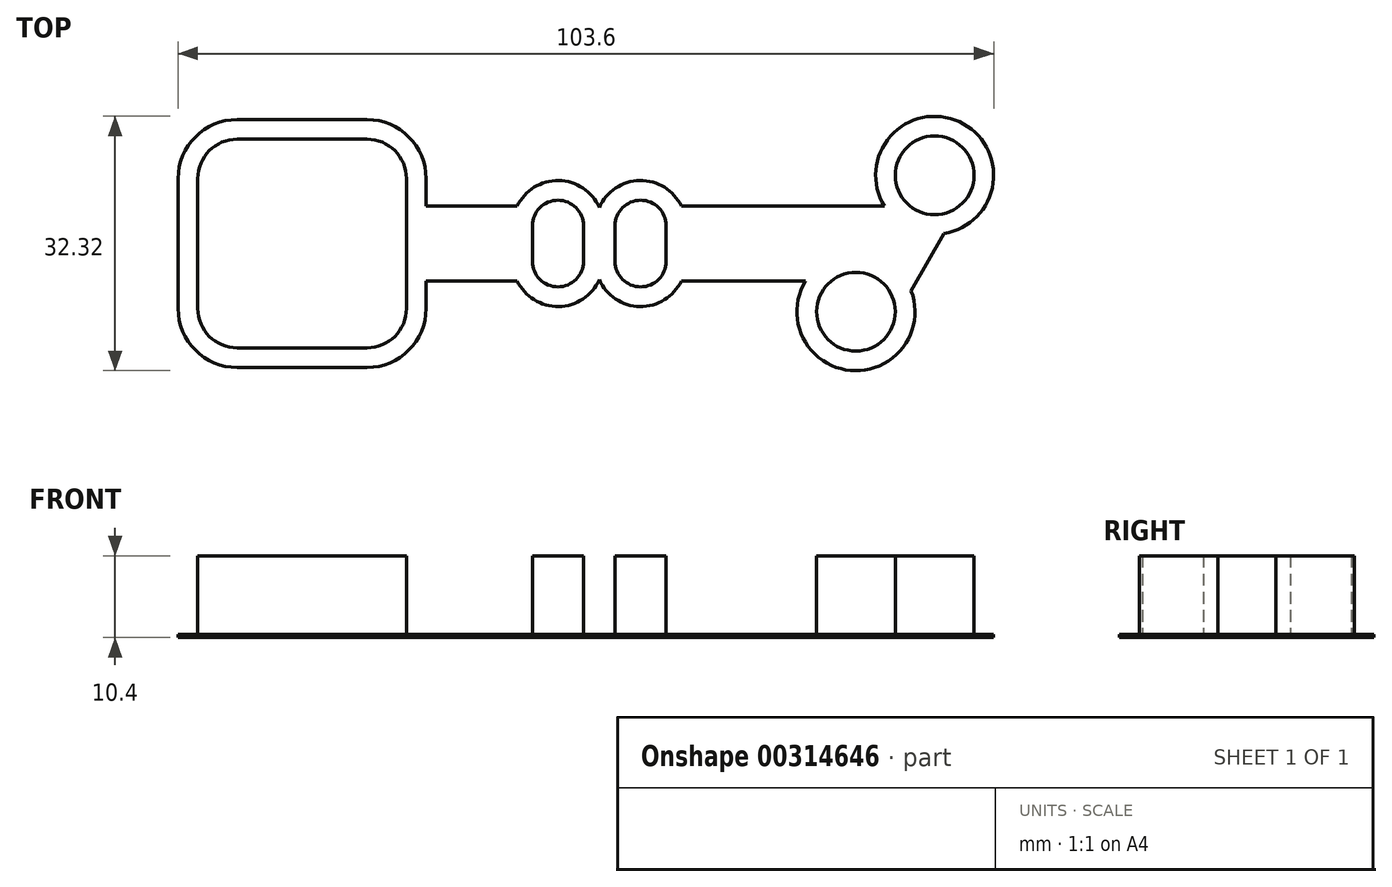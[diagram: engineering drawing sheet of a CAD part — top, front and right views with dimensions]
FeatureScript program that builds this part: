
annotation { "Feature Type Name" : "Feature", "Feature Type Description" : "" }
export const myFeature = defineFeature(function(context is Context, id is Id, definition is map)
    precondition{}
    {
        {
            var Q0;
            Q0=qCreatedBy(makeId("Top.planeOp"),FACE);
            var sketch = newSketch(context, id + "F0", { "sketchPlane" : qUnion([Q0])});
            skLineSegment(sketch, "E0.bottom", {"start": v(8.25, -13.25) * mm, "end": v(-8.25, -13.25) * mm});
            skLineSegment(sketch, "E0.top", {"start": v(8.25, 13.25) * mm, "end": v(-8.25, 13.25) * mm});
            skLineSegment(sketch, "E0.left", {"start": v(13.25, -8.25) * mm, "end": v(13.25, -4.5) * mm});
            skLineSegment(sketch, "E0.right", {"start": v(-13.25, -8.25) * mm, "end": v(-13.25, 8.25) * mm});
            skPoint(sketch, "E0.middle", {"position": v(0, 0) * mm});
            skPoint(sketch, "E1.visualSharp", {"position": v(-13.25, 13.25) * mm});
            skArc(sketch, "E1.filletArc", {"start": v(-8.25, 13.25) * mm, "mid": v(-11.79, 11.79) * mm, "end": v(-13.25, 8.25) * mm});
            skPoint(sketch, "E2.visualSharp", {"position": v(13.25, 13.25) * mm});
            skArc(sketch, "E2.filletArc", {"start": v(13.25, 8.25) * mm, "mid": v(11.79, 11.79) * mm, "end": v(8.25, 13.25) * mm});
            skPoint(sketch, "E3.visualSharp", {"position": v(13.25, -13.25) * mm});
            skArc(sketch, "E3.filletArc", {"start": v(8.25, -13.25) * mm, "mid": v(11.79, -11.79) * mm, "end": v(13.25, -8.25) * mm});
            skPoint(sketch, "E4.visualSharp", {"position": v(-13.25, -13.25) * mm});
            skArc(sketch, "E4.filletArc", {"start": v(-13.25, -8.25) * mm, "mid": v(-11.79, -11.79) * mm, "end": v(-8.25, -13.25) * mm});
            skCircle(sketch, "E5", {"center": v(0, 0) * mm, "radius": 4.5 * mm});
            skLineSegment(sketch, "E6", {"start": v(-4.5, 13.25) * mm, "end": v(-4.5, -13.25) * mm});
            skLineSegment(sketch, "E7", {"start": v(4.5, 13.25) * mm, "end": v(4.5, -13.25) * mm});
            skLineSegment(sketch, "E8", {"start": v(-13.25, 4.5) * mm, "end": v(13.25, 4.5) * mm});
            skLineSegment(sketch, "E9", {"start": v(-13.25, -4.5) * mm, "end": v(13.25, -4.5) * mm});
            skPoint(sketch, "E10.endSnap0", {"position": v(-4.5, 0) * mm});
            skLineSegment(sketch, "E11", {"start": v(13.25, 2.25) * mm, "end": v(29.25, 2.25) * mm});
            skLineSegment(sketch, "E12.bottom", {"start": v(29.25, 2.25) * mm, "end": v(35.75, 2.25) * mm});
            skLineSegment(sketch, "E12.top", {"start": v(29.25, -2.25) * mm, "end": v(35.75, -2.25) * mm});
            skLineSegment(sketch, "E12.left", {"start": v(29.25, 2.25) * mm, "end": v(29.25, -2.25) * mm});
            skLineSegment(sketch, "E12.right", {"start": v(35.75, 2.25) * mm, "end": v(35.75, -2.25) * mm});
            skLineSegment(sketch, "E13", {"start": v(37.75, 6.12) * mm, "end": v(37.75, -11.41) * mm, "construction": true});
            skLineSegment(sketch, "E14.MirrorCS", {"start": v(13.25, -2.25) * mm, "end": v(29.25, -2.25) * mm});
            skLineSegment(sketch, "E15.MirrorCS", {"start": v(39.75, 2.25) * mm, "end": v(39.75, -2.25) * mm});
            skLineSegment(sketch, "E16.MirrorCS", {"start": v(46.25, 2.25) * mm, "end": v(39.75, 2.25) * mm});
            skLineSegment(sketch, "E17.MirrorCS", {"start": v(85.23, 0) * mm, "end": v(-26.26, 0) * mm, "construction": true});
            skLineSegment(sketch, "E18.MirrorCS", {"start": v(46.25, -2.25) * mm, "end": v(39.75, -2.25) * mm});
            skLineSegment(sketch, "E19.MirrorCS", {"start": v(46.25, 2.25) * mm, "end": v(46.25, -2.25) * mm});
            skLineSegment(sketch, "E20", {"start": v(35.75, 2.25) * mm, "end": v(39.75, 2.25) * mm});
            skLineSegment(sketch, "E21", {"start": v(39.75, -2.25) * mm, "end": v(35.75, -2.25) * mm});
            skPoint(sketch, "E22", {"position": v(4.5, 0) * mm});
            skArc(sketch, "E23", {"start": v(29.25, 2.25) * mm, "mid": v(32.5, 5.5) * mm, "end": v(35.75, 2.25) * mm});
            skArc(sketch, "E24.MirrorCS", {"start": v(29.25, -2.25) * mm, "mid": v(32.5, -5.5) * mm, "end": v(35.75, -2.25) * mm});
            skArc(sketch, "E25.MirrorCS", {"start": v(46.25, 2.25) * mm, "mid": v(43, 5.5) * mm, "end": v(39.75, 2.25) * mm});
            skArc(sketch, "E26.MirrorCS", {"start": v(46.25, -2.25) * mm, "mid": v(43, -5.5) * mm, "end": v(39.75, -2.25) * mm});
            skLineSegment(sketch, "E27", {"start": v(80.35, 8.66) * mm, "end": v(70.35, -8.66) * mm, "construction": true});
            skPoint(sketch, "E28", {"position": v(75.35, 0) * mm});
            skLineSegment(sketch, "E29", {"start": v(76.17, 5.92) * mm, "end": v(76.17, 5.92) * mm});
            skLineSegment(sketch, "E30.MirrorCS", {"start": v(80.06, 3.67) * mm, "end": v(74.53, -5.92) * mm});
            skPoint(sketch, "E31", {"position": v(72.75, 0) * mm});
            skLineSegment(sketch, "E32", {"start": v(46.25, 2.25) * mm, "end": v(74.05, 2.25) * mm});
            skLineSegment(sketch, "E33", {"start": v(46.25, -2.25) * mm, "end": v(71.45, -2.25) * mm});
            skLineSegment(sketch, "E34", {"start": v(13.25, 4.5) * mm, "end": v(13.25, 8.25) * mm});
            skLineSegment(sketch, "E35", {"start": v(13.25, 2.25) * mm, "end": v(13.25, 4.5) * mm});
            skLineSegment(sketch, "E36", {"start": v(13.25, -2.25) * mm, "end": v(13.25, 2.25) * mm});
            skLineSegment(sketch, "E37", {"start": v(13.25, -4.5) * mm, "end": v(13.25, -2.25) * mm});
            skLineSegment(sketch, "E38", {"start": v(74.05, 2.25) * mm, "end": v(71.45, -2.25) * mm});
            skLineSegment(sketch, "E39", {"start": v(71.45, -2.25) * mm, "end": v(71.45, -2.25) * mm});
            skLineSegment(sketch, "E40", {"start": v(76.17, 5.92) * mm, "end": v(74.05, 2.25) * mm});
            skArc(sketch, "E41", {"start": v(76.17, 5.92) * mm, "mid": v(77.85, 4.33) * mm, "end": v(80.06, 3.67) * mm});
            skArc(sketch, "E42", {"start": v(76.1, 11.31) * mm, "mid": v(75.35, 8.6) * mm, "end": v(76.17, 5.92) * mm});
            skArc(sketch, "E43", {"start": v(80.06, 3.67) * mm, "mid": v(84.79, 10.96) * mm, "end": v(76.1, 11.31) * mm});
            skLineSegment(sketch, "E44", {"start": v(76.1, 11.31) * mm, "end": v(76.1, 11.31) * mm});
            skArc(sketch, "E45", {"start": v(74.53, -5.92) * mm, "mid": v(72.85, -4.33) * mm, "end": v(70.63, -3.67) * mm});
            skLineSegment(sketch, "E46", {"start": v(74.94, -10.64) * mm, "end": v(74.94, -10.64) * mm});
            skArc(sketch, "E47", {"start": v(74.94, -10.64) * mm, "mid": v(75.33, -8.23) * mm, "end": v(74.53, -5.92) * mm});
            skArc(sketch, "E48", {"start": v(70.63, -3.67) * mm, "mid": v(66.1, -11.29) * mm, "end": v(74.94, -10.64) * mm});
            skLineSegment(sketch, "E49", {"start": v(70.63, -3.67) * mm, "end": v(70.63, -3.67) * mm});
            skLineSegment(sketch, "E50", {"start": v(71.45, -2.25) * mm, "end": v(70.63, -3.67) * mm});
            skArc(sketch, "E51.0", {"start": v(15.75, 8.25) * mm, "mid": v(13.55, 13.55) * mm, "end": v(8.25, 15.75) * mm});
            skLineSegment(sketch, "E51.1", {"start": v(15.75, 4.75) * mm, "end": v(15.75, 8.25) * mm});
            skLineSegment(sketch, "E51.2", {"start": v(15.75, 4.75) * mm, "end": v(27.32, 4.75) * mm});
            skArc(sketch, "E51.3", {"start": v(27.32, 4.75) * mm, "mid": v(32.59, 8) * mm, "end": v(37.75, 4.6) * mm});
            skArc(sketch, "E51.4", {"start": v(48.18, 4.75) * mm, "mid": v(42.91, 8) * mm, "end": v(37.75, 4.6) * mm});
            skLineSegment(sketch, "E51.5", {"start": v(8.25, 15.75) * mm, "end": v(-8.25, 15.75) * mm});
            skLineSegment(sketch, "E51.6", {"start": v(48.18, 4.75) * mm, "end": v(73.95, 4.75) * mm});
            skArc(sketch, "E51.7", {"start": v(74, 12.64) * mm, "mid": v(72.85, 8.7) * mm, "end": v(73.95, 4.75) * mm});
            skArc(sketch, "E51.8", {"start": v(81.56, 1.26) * mm, "mid": v(86.6, 12.81) * mm, "end": v(74, 12.64) * mm});
            skLineSegment(sketch, "E51.9", {"start": v(81.56, 1.26) * mm, "end": v(77.36, -6) * mm});
            skArc(sketch, "E51.10", {"start": v(77.23, -11.64) * mm, "mid": v(77.85, -8.83) * mm, "end": v(77.36, -6) * mm});
            skArc(sketch, "E51.11", {"start": v(63.95, -4.75) * mm, "mid": v(66.9, -15.32) * mm, "end": v(77.23, -11.64) * mm});
            skLineSegment(sketch, "E51.12", {"start": v(8.25, -15.75) * mm, "end": v(-8.25, -15.75) * mm});
            skArc(sketch, "E51.13", {"start": v(-15.75, -8.25) * mm, "mid": v(-13.55, -13.55) * mm, "end": v(-8.25, -15.75) * mm});
            skLineSegment(sketch, "E51.14", {"start": v(-15.75, -8.25) * mm, "end": v(-15.75, 8.25) * mm});
            skArc(sketch, "E51.15", {"start": v(-8.25, 15.75) * mm, "mid": v(-13.55, 13.55) * mm, "end": v(-15.75, 8.25) * mm});
            skArc(sketch, "E51.16", {"start": v(8.25, -15.75) * mm, "mid": v(13.55, -13.55) * mm, "end": v(15.75, -8.25) * mm});
            skLineSegment(sketch, "E51.17", {"start": v(15.75, -8.25) * mm, "end": v(15.75, -4.75) * mm});
            skLineSegment(sketch, "E51.18", {"start": v(15.75, -4.75) * mm, "end": v(27.32, -4.75) * mm});
            skArc(sketch, "E51.19", {"start": v(27.32, -4.75) * mm, "mid": v(32.59, -8) * mm, "end": v(37.75, -4.6) * mm});
            skArc(sketch, "E51.20", {"start": v(48.18, -4.75) * mm, "mid": v(42.91, -8) * mm, "end": v(37.75, -4.6) * mm});
            skLineSegment(sketch, "E51.21", {"start": v(48.18, -4.75) * mm, "end": v(63.95, -4.75) * mm});
            skSolve(sketch);
        }
        {
            var Q0;
            {var subQ6=sQuery(id+"F0.wireOp",EDGE,"E2.filletArc");Q0=makeQuery(id+"F0.imprint","IMPRINT",FACE,{"disambiguationData":[TD([[makeQuery(id+"F0.imprint","IMPRINT",EDGE,{"derivedFrom":subQ6}),1.0]])]});}
            var Q1;
            {var subQ5=sQuery(id+"F0.wireOp",EDGE,"E1.filletArc");Q1=makeQuery(id+"F0.imprint","IMPRINT",FACE,{"disambiguationData":[TD([[makeQuery(id+"F0.imprint","IMPRINT",EDGE,{"derivedFrom":subQ5}),1.0]])]});}
            var Q2;
            {var subQ2=sQuery(id+"F0.wireOp",EDGE,"E6");var subQ5=sQuery(id+"F0.wireOp",EDGE,"E0.top");var subQ8=makeQuery(id+"F0.imprint","INTERSECT",VERTEX,{"derivedFrom":[subQ5,subQ2]});Q2=makeQuery(id+"F0.imprint","IMPRINT",FACE,{"disambiguationData":[TD([[makeQuery(id+"F0.imprint","IMPRINT",EDGE,{"disambiguationData":[TD([[subQ8,1.0]])],"derivedFrom":subQ5}),1.0]])]});}
            var Q3;
            {var subQ0=sQuery(id+"F0.wireOp",EDGE,"E8");var subQ1=sQuery(id+"F0.wireOp",EDGE,"E0.right");var subQ2=makeQuery(id+"F0.imprint","INTERSECT",VERTEX,{"derivedFrom":[subQ1,subQ0]});Q3=makeQuery(id+"F0.imprint","IMPRINT",FACE,{"disambiguationData":[TD([[makeQuery(id+"F0.imprint","IMPRINT",EDGE,{"disambiguationData":[TD([[subQ2,1.0]])],"derivedFrom":subQ1}),-1.0]])]});}
            var Q4;
            Q4=makeQuery(id+"F0.imprint","IMPRINT",FACE,{"disambiguationData":[TD([[makeQuery(id+"F0.imprint","IMPRINT",EDGE,{"derivedFrom":sQuery(id+"F0.wireOp",EDGE,"E12.top")}),-1.0]])]});
            var Q5;
            Q5=makeQuery(id+"F0.imprint","IMPRINT",FACE,{"disambiguationData":[TD([[makeQuery(id+"F0.imprint","IMPRINT",EDGE,{"derivedFrom":sQuery(id+"F0.wireOp",EDGE,"E11")}),-1.0]])]});
            var Q6;
            Q6=makeQuery(id+"F0.imprint","IMPRINT",FACE,{"disambiguationData":[TD([[makeQuery(id+"F0.imprint","IMPRINT",EDGE,{"derivedFrom":sQuery(id+"F0.wireOp",EDGE,"E12.bottom")}),1.0]])]});
            var Q7;
            Q7=makeQuery(id+"F0.imprint","IMPRINT",FACE,{"disambiguationData":[TD([[makeQuery(id+"F0.imprint","IMPRINT",EDGE,{"derivedFrom":sQuery(id+"F0.wireOp",EDGE,"E18.MirrorCS")}),1.0]])]});
            var Q8;
            {var subQ0=sQuery(id+"F0.wireOp",EDGE,"E35");Q8=makeQuery(id+"F0.imprint","IMPRINT",FACE,{"disambiguationData":[TD([[makeQuery(id+"F0.imprint","IMPRINT",EDGE,{"derivedFrom":subQ0}),1.0]])]});}
            var Q9;
            {var subQ1=sQuery(id+"F0.wireOp",EDGE,"E0.left");Q9=makeQuery(id+"F0.imprint","IMPRINT",FACE,{"disambiguationData":[TD([[makeQuery(id+"F0.imprint","IMPRINT",EDGE,{"derivedFrom":subQ1}),1.0]])]});}
            var Q10;
            {var subQ5=sQuery(id+"F0.wireOp",EDGE,"E4.filletArc");Q10=makeQuery(id+"F0.imprint","IMPRINT",FACE,{"disambiguationData":[TD([[makeQuery(id+"F0.imprint","IMPRINT",EDGE,{"derivedFrom":subQ5}),1.0]])]});}
            var Q11;
            Q11=makeQuery(id+"F0.imprint","IMPRINT",FACE,{"disambiguationData":[TD([[makeQuery(id+"F0.imprint","IMPRINT",EDGE,{"derivedFrom":sQuery(id+"F0.wireOp",EDGE,"E45")}),1.0]])]});
            var Q12;
            Q12=makeQuery(id+"F0.imprint","IMPRINT",FACE,{"disambiguationData":[TD([[makeQuery(id+"F0.imprint","IMPRINT",EDGE,{"derivedFrom":sQuery(id+"F0.wireOp",EDGE,"E0.left")}),-1.0]])]});
            var Q13;
            Q13=makeQuery(id+"F0.imprint","IMPRINT",FACE,{"disambiguationData":[TD([[makeQuery(id+"F0.imprint","IMPRINT",EDGE,{"derivedFrom":sQuery(id+"F0.wireOp",EDGE,"E41")}),1.0]])]});
            var Q14;
            Q14=makeQuery(id+"F0.imprint","IMPRINT",FACE,{"disambiguationData":[TD([[makeQuery(id+"F0.imprint","IMPRINT",EDGE,{"derivedFrom":sQuery(id+"F0.wireOp",EDGE,"E19.MirrorCS")}),1.0]])]});
            var Q15;
            Q15=makeQuery(id+"F0.imprint","IMPRINT",FACE,{"disambiguationData":[TD([[makeQuery(id+"F0.imprint","IMPRINT",EDGE,{"derivedFrom":sQuery(id+"F0.wireOp",EDGE,"E16.MirrorCS")}),-1.0]])]});
            var Q16;
            {var subQ1=sQuery(id+"F0.wireOp",EDGE,"E0.bottom");var subQ6=sQuery(id+"F0.wireOp",EDGE,"E6");var subQ8=makeQuery(id+"F0.imprint","INTERSECT",VERTEX,{"derivedFrom":[subQ1,subQ6]});Q16=makeQuery(id+"F0.imprint","IMPRINT",FACE,{"disambiguationData":[TD([[makeQuery(id+"F0.imprint","IMPRINT",EDGE,{"disambiguationData":[TD([[subQ8,1.0]])],"derivedFrom":subQ1}),-1.0]])]});}
            var Q17;
            Q17=makeQuery(id+"F0.imprint","IMPRINT",FACE,{"disambiguationData":[TD([[makeQuery(id+"F0.imprint","IMPRINT",EDGE,{"derivedFrom":sQuery(id+"F0.wireOp",EDGE,"E30.MirrorCS")}),-1.0]])]});
            var Q18;
            {var subQ0=sQuery(id+"F0.wireOp",EDGE,"E5");var subQ1=makeQuery(id+"F0.imprint","INTERSECT",VERTEX,{"derivedFrom":[subQ0,sQuery(id+"F0.wireOp",EDGE,"E8")]});Q18=makeQuery(id+"F0.imprint","IMPRINT",FACE,{"disambiguationData":[TD([[makeQuery(id+"F0.imprint","IMPRINT",EDGE,{"disambiguationData":[TD([[subQ1,1.0]])],"derivedFrom":subQ0}),1.0]])]});}
            var Q19;
            {var subQ0=sQuery(id+"F0.wireOp",EDGE,"E7");var subQ1=sQuery(id+"F0.wireOp",EDGE,"E5");var subQ2=makeQuery(id+"F0.imprint","INTERSECT",VERTEX,{"derivedFrom":[subQ1,subQ0]});Q19=makeQuery(id+"F0.imprint","IMPRINT",FACE,{"disambiguationData":[TD([[makeQuery(id+"F0.imprint","IMPRINT",EDGE,{"disambiguationData":[TD([[subQ2,1.0]])],"derivedFrom":subQ1}),-1.0]])]});}
            var Q20;
            {var subQ0=sQuery(id+"F0.wireOp",EDGE,"E8");var subQ1=sQuery(id+"F0.wireOp",EDGE,"E5");var subQ2=makeQuery(id+"F0.imprint","INTERSECT",VERTEX,{"derivedFrom":[subQ1,subQ0]});Q20=makeQuery(id+"F0.imprint","IMPRINT",FACE,{"disambiguationData":[TD([[makeQuery(id+"F0.imprint","IMPRINT",EDGE,{"disambiguationData":[TD([[subQ2,-1.0]])],"derivedFrom":subQ1}),-1.0]])]});}
            var Q21;
            {var subQ0=sQuery(id+"F0.wireOp",EDGE,"E6");var subQ1=sQuery(id+"F0.wireOp",EDGE,"E5");var subQ2=makeQuery(id+"F0.imprint","INTERSECT",VERTEX,{"derivedFrom":[subQ1,subQ0]});Q21=makeQuery(id+"F0.imprint","IMPRINT",FACE,{"disambiguationData":[TD([[makeQuery(id+"F0.imprint","IMPRINT",EDGE,{"disambiguationData":[TD([[subQ2,-1.0]])],"derivedFrom":subQ1}),-1.0]])]});}
            var Q22;
            {var subQ0=sQuery(id+"F0.wireOp",EDGE,"E8");var subQ1=sQuery(id+"F0.wireOp",EDGE,"E5");var subQ2=makeQuery(id+"F0.imprint","INTERSECT",VERTEX,{"derivedFrom":[subQ1,subQ0]});Q22=makeQuery(id+"F0.imprint","IMPRINT",FACE,{"disambiguationData":[TD([[makeQuery(id+"F0.imprint","IMPRINT",EDGE,{"disambiguationData":[TD([[subQ2,1.0]])],"derivedFrom":subQ1}),-1.0]])]});}
            var Q23;
            Q23=makeQuery(id+"F0.imprint","IMPRINT",FACE,{"disambiguationData":[TD([[makeQuery(id+"F0.imprint","IMPRINT",EDGE,{"derivedFrom":sQuery(id+"F0.wireOp",EDGE,"E12.bottom")}),-1.0]])]});
            var Q24;
            Q24=makeQuery(id+"F0.imprint","IMPRINT",FACE,{"disambiguationData":[TD([[makeQuery(id+"F0.imprint","IMPRINT",EDGE,{"derivedFrom":sQuery(id+"F0.wireOp",EDGE,"E12.right")}),1.0]])]});
            var Q25;
            Q25=makeQuery(id+"F0.imprint","IMPRINT",FACE,{"disambiguationData":[TD([[makeQuery(id+"F0.imprint","IMPRINT",EDGE,{"derivedFrom":sQuery(id+"F0.wireOp",EDGE,"E16.MirrorCS")}),1.0]])]});
            extrude(context, id + "F1", {"entities" : qUnion([Q0, Q1, Q2, Q3, Q4, Q5, Q6, Q7, Q8, Q9, Q10, Q11, Q12, Q13, Q14, Q15, Q16, Q17, Q18, Q19, Q20, Q21, Q22, Q23, Q24, Q25]), "depth" : 0.4 * mm});
        }
        {
            var Q0;
            Q0=makeQuery(id+"F1.opExtrude","CAP_FACE",FACE,{"disambiguationData":[OSD([sQuery(id+"F0.wireOp",EDGE,"E51.0"),sQuery(id+"F0.wireOp",EDGE,"E51.1"),sQuery(id+"F0.wireOp",EDGE,"E51.2"),sQuery(id+"F0.wireOp",EDGE,"E51.3"),sQuery(id+"F0.wireOp",EDGE,"E51.4"),sQuery(id+"F0.wireOp",EDGE,"E51.5"),sQuery(id+"F0.wireOp",EDGE,"E51.6"),sQuery(id+"F0.wireOp",EDGE,"E51.7"),sQuery(id+"F0.wireOp",EDGE,"E51.8"),sQuery(id+"F0.wireOp",EDGE,"E51.9"),sQuery(id+"F0.wireOp",EDGE,"E51.10"),sQuery(id+"F0.wireOp",EDGE,"E51.11"),sQuery(id+"F0.wireOp",EDGE,"E51.12"),sQuery(id+"F0.wireOp",EDGE,"E51.13"),sQuery(id+"F0.wireOp",EDGE,"E51.14"),sQuery(id+"F0.wireOp",EDGE,"E51.15"),sQuery(id+"F0.wireOp",EDGE,"E51.16"),sQuery(id+"F0.wireOp",EDGE,"E51.17"),sQuery(id+"F0.wireOp",EDGE,"E51.18"),sQuery(id+"F0.wireOp",EDGE,"E51.19"),sQuery(id+"F0.wireOp",EDGE,"E51.20"),sQuery(id+"F0.wireOp",EDGE,"E51.21")])],"isStart":false});
            var sketch = newSketch(context, id + "F2", { "sketchPlane" : qUnion([Q0])});
            skLineSegment(sketch, "E52.0", {"start": v(8.25, -13.25) * mm, "end": v(-8.25, -13.25) * mm});
            skLineSegment(sketch, "E52.1", {"start": v(8.25, 13.25) * mm, "end": v(-8.25, 13.25) * mm});
            skLineSegment(sketch, "E52.2", {"start": v(13.25, -8.25) * mm, "end": v(13.25, -4.5) * mm});
            skLineSegment(sketch, "E52.3", {"start": v(-13.25, -8.25) * mm, "end": v(-13.25, 8.25) * mm});
            skPoint(sketch, "E52.4", {"position": v(0, 0) * mm});
            skPoint(sketch, "E52.5", {"position": v(-13.25, 13.25) * mm});
            skArc(sketch, "E52.6", {"start": v(-8.25, 13.25) * mm, "mid": v(-11.79, 11.79) * mm, "end": v(-13.25, 8.25) * mm});
            skPoint(sketch, "E52.7", {"position": v(13.25, 13.25) * mm});
            skArc(sketch, "E52.8", {"start": v(13.25, 8.25) * mm, "mid": v(11.79, 11.79) * mm, "end": v(8.25, 13.25) * mm});
            skPoint(sketch, "E52.9", {"position": v(13.25, -13.25) * mm});
            skArc(sketch, "E52.10", {"start": v(8.25, -13.25) * mm, "mid": v(11.79, -11.79) * mm, "end": v(13.25, -8.25) * mm});
            skPoint(sketch, "E52.11", {"position": v(-13.25, -13.25) * mm});
            skArc(sketch, "E52.12", {"start": v(-13.25, -8.25) * mm, "mid": v(-11.79, -11.79) * mm, "end": v(-8.25, -13.25) * mm});
            skCircle(sketch, "E52.13", {"center": v(0, 0) * mm, "radius": 4.5 * mm});
            skLineSegment(sketch, "E52.14", {"start": v(-4.5, 13.25) * mm, "end": v(-4.5, -13.25) * mm});
            skLineSegment(sketch, "E52.15", {"start": v(4.5, 13.25) * mm, "end": v(4.5, -13.25) * mm});
            skLineSegment(sketch, "E52.16", {"start": v(-13.25, 4.5) * mm, "end": v(13.25, 4.5) * mm});
            skLineSegment(sketch, "E52.17", {"start": v(-13.25, -4.5) * mm, "end": v(13.25, -4.5) * mm});
            skPoint(sketch, "E52.18", {"position": v(-4.5, 0) * mm});
            skLineSegment(sketch, "E52.19", {"start": v(13.25, 2.25) * mm, "end": v(29.25, 2.25) * mm});
            skLineSegment(sketch, "E52.20", {"start": v(29.25, 2.25) * mm, "end": v(35.75, 2.25) * mm});
            skLineSegment(sketch, "E52.21", {"start": v(29.25, -2.25) * mm, "end": v(35.75, -2.25) * mm});
            skLineSegment(sketch, "E52.22", {"start": v(29.25, 2.25) * mm, "end": v(29.25, -2.25) * mm});
            skLineSegment(sketch, "E52.23", {"start": v(35.75, 2.25) * mm, "end": v(35.75, -2.25) * mm});
            skLineSegment(sketch, "E52.25", {"start": v(13.25, -2.25) * mm, "end": v(29.25, -2.25) * mm});
            skLineSegment(sketch, "E52.26", {"start": v(39.75, 2.25) * mm, "end": v(39.75, -2.25) * mm});
            skLineSegment(sketch, "E52.27", {"start": v(46.25, 2.25) * mm, "end": v(39.75, 2.25) * mm});
            skLineSegment(sketch, "E52.29", {"start": v(39.75, 2.25) * mm, "end": v(39.75, -2.25) * mm});
            skLineSegment(sketch, "E52.30", {"start": v(46.25, -2.25) * mm, "end": v(39.75, -2.25) * mm});
            skLineSegment(sketch, "E52.31", {"start": v(46.25, 2.25) * mm, "end": v(46.25, -2.25) * mm});
            skLineSegment(sketch, "E52.32", {"start": v(35.75, 2.25) * mm, "end": v(39.75, 2.25) * mm});
            skLineSegment(sketch, "E52.33", {"start": v(39.75, -2.25) * mm, "end": v(35.75, -2.25) * mm});
            skPoint(sketch, "E52.34", {"position": v(4.5, 0) * mm});
            skArc(sketch, "E52.35", {"start": v(29.25, 2.25) * mm, "mid": v(32.5, 5.5) * mm, "end": v(35.75, 2.25) * mm});
            skArc(sketch, "E52.36", {"start": v(29.25, -2.25) * mm, "mid": v(32.5, -5.5) * mm, "end": v(35.75, -2.25) * mm});
            skArc(sketch, "E52.37", {"start": v(46.25, 2.25) * mm, "mid": v(43, 5.5) * mm, "end": v(39.75, 2.25) * mm});
            skArc(sketch, "E52.38", {"start": v(46.25, -2.25) * mm, "mid": v(43, -5.5) * mm, "end": v(39.75, -2.25) * mm});
            skArc(sketch, "E52.39", {"start": v(46.25, 2.25) * mm, "mid": v(43, 5.5) * mm, "end": v(39.75, 2.25) * mm});
            skLineSegment(sketch, "E52.40", {"start": v(80.35, 8.66) * mm, "end": v(70.35, -8.66) * mm});
            skPoint(sketch, "E52.41", {"position": v(75.35, 0) * mm});
            skPoint(sketch, "E52.42", {"position": v(76.17, 5.92) * mm});
            skLineSegment(sketch, "E52.43", {"start": v(80.06, 3.67) * mm, "end": v(74.53, -5.92) * mm});
            skPoint(sketch, "E52.44", {"position": v(72.75, 0) * mm});
            skLineSegment(sketch, "E52.45", {"start": v(46.25, 2.25) * mm, "end": v(74.05, 2.25) * mm});
            skLineSegment(sketch, "E52.46", {"start": v(46.25, -2.25) * mm, "end": v(71.45, -2.25) * mm});
            skLineSegment(sketch, "E52.47", {"start": v(13.25, 4.5) * mm, "end": v(13.25, 8.25) * mm});
            skLineSegment(sketch, "E52.48", {"start": v(13.25, 2.25) * mm, "end": v(13.25, 4.5) * mm});
            skLineSegment(sketch, "E52.49", {"start": v(13.25, -2.25) * mm, "end": v(13.25, 2.25) * mm});
            skLineSegment(sketch, "E52.50", {"start": v(13.25, -4.5) * mm, "end": v(13.25, -2.25) * mm});
            skLineSegment(sketch, "E52.51", {"start": v(74.05, 2.25) * mm, "end": v(71.45, -2.25) * mm});
            skPoint(sketch, "E52.52", {"position": v(71.45, -2.25) * mm});
            skLineSegment(sketch, "E52.53", {"start": v(76.17, 5.92) * mm, "end": v(74.05, 2.25) * mm});
            skArc(sketch, "E52.54", {"start": v(76.17, 5.92) * mm, "mid": v(77.85, 4.33) * mm, "end": v(80.06, 3.67) * mm});
            skArc(sketch, "E52.55", {"start": v(76.1, 11.31) * mm, "mid": v(75.35, 8.6) * mm, "end": v(76.17, 5.92) * mm});
            skArc(sketch, "E52.56", {"start": v(80.06, 3.67) * mm, "mid": v(84.79, 10.96) * mm, "end": v(76.1, 11.31) * mm});
            skPoint(sketch, "E52.57", {"position": v(80.35, 8.66) * mm});
            skArc(sketch, "E52.58", {"start": v(74.53, -5.92) * mm, "mid": v(72.85, -4.33) * mm, "end": v(70.63, -3.67) * mm});
            skPoint(sketch, "E52.59", {"position": v(70.35, -8.66) * mm});
            skArc(sketch, "E52.60", {"start": v(74.94, -10.64) * mm, "mid": v(75.33, -8.23) * mm, "end": v(74.53, -5.92) * mm});
            skArc(sketch, "E52.61", {"start": v(70.63, -3.67) * mm, "mid": v(66.1, -11.29) * mm, "end": v(74.94, -10.64) * mm});
            skPoint(sketch, "E52.62", {"position": v(70.63, -3.67) * mm});
            skLineSegment(sketch, "E52.63", {"start": v(71.45, -2.25) * mm, "end": v(70.63, -3.67) * mm});
            skArc(sketch, "E52.64", {"start": v(15.75, 8.25) * mm, "mid": v(13.55, 13.55) * mm, "end": v(8.25, 15.75) * mm});
            skLineSegment(sketch, "E52.65", {"start": v(15.75, 4.75) * mm, "end": v(15.75, 8.25) * mm});
            skLineSegment(sketch, "E52.66", {"start": v(15.75, 4.75) * mm, "end": v(27.32, 4.75) * mm});
            skArc(sketch, "E52.67", {"start": v(27.32, 4.75) * mm, "mid": v(32.59, 8) * mm, "end": v(37.75, 4.6) * mm});
            skArc(sketch, "E52.68", {"start": v(48.18, 4.75) * mm, "mid": v(42.91, 8) * mm, "end": v(37.75, 4.6) * mm});
            skLineSegment(sketch, "E52.69", {"start": v(8.25, 15.75) * mm, "end": v(-8.25, 15.75) * mm});
            skLineSegment(sketch, "E52.70", {"start": v(48.18, 4.75) * mm, "end": v(73.95, 4.75) * mm});
            skArc(sketch, "E52.71", {"start": v(74, 12.64) * mm, "mid": v(72.85, 8.7) * mm, "end": v(73.95, 4.75) * mm});
            skArc(sketch, "E52.72", {"start": v(81.56, 1.26) * mm, "mid": v(86.6, 12.81) * mm, "end": v(74, 12.64) * mm});
            skLineSegment(sketch, "E52.73", {"start": v(81.56, 1.26) * mm, "end": v(77.36, -6) * mm});
            skArc(sketch, "E52.74", {"start": v(77.23, -11.64) * mm, "mid": v(77.85, -8.83) * mm, "end": v(77.36, -6) * mm});
            skArc(sketch, "E52.75", {"start": v(63.95, -4.75) * mm, "mid": v(66.9, -15.32) * mm, "end": v(77.23, -11.64) * mm});
            skLineSegment(sketch, "E52.76", {"start": v(8.25, -15.75) * mm, "end": v(-8.25, -15.75) * mm});
            skArc(sketch, "E52.77", {"start": v(-15.75, -8.25) * mm, "mid": v(-13.55, -13.55) * mm, "end": v(-8.25, -15.75) * mm});
            skLineSegment(sketch, "E52.78", {"start": v(-15.75, -8.25) * mm, "end": v(-15.75, 8.25) * mm});
            skArc(sketch, "E52.79", {"start": v(-8.25, 15.75) * mm, "mid": v(-13.55, 13.55) * mm, "end": v(-15.75, 8.25) * mm});
            skArc(sketch, "E52.80", {"start": v(8.25, -15.75) * mm, "mid": v(13.55, -13.55) * mm, "end": v(15.75, -8.25) * mm});
            skLineSegment(sketch, "E52.81", {"start": v(15.75, -8.25) * mm, "end": v(15.75, -4.75) * mm});
            skLineSegment(sketch, "E52.82", {"start": v(15.75, -4.75) * mm, "end": v(27.32, -4.75) * mm});
            skArc(sketch, "E52.83", {"start": v(27.32, -4.75) * mm, "mid": v(32.59, -8) * mm, "end": v(37.75, -4.6) * mm});
            skArc(sketch, "E52.84", {"start": v(48.18, -4.75) * mm, "mid": v(42.91, -8) * mm, "end": v(37.75, -4.6) * mm});
            skLineSegment(sketch, "E52.85", {"start": v(48.18, -4.75) * mm, "end": v(63.95, -4.75) * mm});
            skSolve(sketch);
        }
        {
            var Q0;
            {var subQ1=sQuery(id+"F2.wireOp",EDGE,"E52.0");var subQ6=sQuery(id+"F2.wireOp",EDGE,"E52.14");var subQ8=makeQuery(id+"F2.imprint","INTERSECT",VERTEX,{"derivedFrom":[subQ1,subQ6]});Q0=makeQuery(id+"F2.imprint","IMPRINT",FACE,{"disambiguationData":[TD([[makeQuery(id+"F2.imprint","IMPRINT",EDGE,{"disambiguationData":[TD([[subQ8,1.0]])],"derivedFrom":subQ1}),-1.0]])]});}
            var Q1;
            Q1=makeQuery(id+"F2.imprint","IMPRINT",FACE,{"disambiguationData":[TD([[makeQuery(id+"F2.imprint","IMPRINT",EDGE,{"derivedFrom":sQuery(id+"F2.wireOp",EDGE,"E52.21")}),-1.0]])]});
            var Q2;
            Q2=makeQuery(id+"F2.imprint","IMPRINT",FACE,{"disambiguationData":[TD([[makeQuery(id+"F2.imprint","IMPRINT",EDGE,{"derivedFrom":sQuery(id+"F2.wireOp",EDGE,"E52.20")}),1.0]])]});
            var Q3;
            Q3=makeQuery(id+"F2.imprint","IMPRINT",FACE,{"disambiguationData":[TD([[makeQuery(id+"F2.imprint","IMPRINT",EDGE,{"derivedFrom":sQuery(id+"F2.wireOp",EDGE,"E52.20")}),-1.0]])]});
            var Q4;
            Q4=makeQuery(id+"F2.imprint","IMPRINT",FACE,{"disambiguationData":[TD([[makeQuery(id+"F2.imprint","IMPRINT",EDGE,{"derivedFrom":sQuery(id+"F2.wireOp",EDGE,"E52.27")}),-1.0]])]});
            var Q5;
            Q5=makeQuery(id+"F2.imprint","IMPRINT",FACE,{"disambiguationData":[TD([[makeQuery(id+"F2.imprint","IMPRINT",EDGE,{"derivedFrom":sQuery(id+"F2.wireOp",EDGE,"E52.27")}),1.0]])]});
            var Q6;
            Q6=makeQuery(id+"F2.imprint","IMPRINT",FACE,{"disambiguationData":[TD([[makeQuery(id+"F2.imprint","IMPRINT",EDGE,{"derivedFrom":sQuery(id+"F2.wireOp",EDGE,"E52.30")}),1.0]])]});
            var Q7;
            {var subQ0=sQuery(id+"F2.wireOp",EDGE,"E52.60");Q7=makeQuery(id+"F2.imprint","IMPRINT",FACE,{"disambiguationData":[TD([[makeQuery(id+"F2.imprint","IMPRINT",EDGE,{"derivedFrom":subQ0}),1.0]])]});}
            var Q8;
            {var subQ0=sQuery(id+"F2.wireOp",EDGE,"E52.55");Q8=makeQuery(id+"F2.imprint","IMPRINT",FACE,{"disambiguationData":[TD([[makeQuery(id+"F2.imprint","IMPRINT",EDGE,{"derivedFrom":subQ0}),1.0]])]});}
            var Q9;
            {var subQ0=sQuery(id+"F2.wireOp",EDGE,"E52.16");var subQ1=sQuery(id+"F2.wireOp",EDGE,"E52.3");var subQ2=makeQuery(id+"F2.imprint","INTERSECT",VERTEX,{"derivedFrom":[subQ1,subQ0]});Q9=makeQuery(id+"F2.imprint","IMPRINT",FACE,{"disambiguationData":[TD([[makeQuery(id+"F2.imprint","IMPRINT",EDGE,{"disambiguationData":[TD([[subQ2,1.0]])],"derivedFrom":subQ1}),-1.0]])]});}
            var Q10;
            {var subQ0=sQuery(id+"F2.wireOp",EDGE,"E52.48");Q10=makeQuery(id+"F2.imprint","IMPRINT",FACE,{"disambiguationData":[TD([[makeQuery(id+"F2.imprint","IMPRINT",EDGE,{"derivedFrom":subQ0}),1.0]])]});}
            var Q11;
            {var subQ2=sQuery(id+"F2.wireOp",EDGE,"E52.14");var subQ5=sQuery(id+"F2.wireOp",EDGE,"E52.1");var subQ8=makeQuery(id+"F2.imprint","INTERSECT",VERTEX,{"derivedFrom":[subQ5,subQ2]});Q11=makeQuery(id+"F2.imprint","IMPRINT",FACE,{"disambiguationData":[TD([[makeQuery(id+"F2.imprint","IMPRINT",EDGE,{"disambiguationData":[TD([[subQ8,1.0]])],"derivedFrom":subQ5}),1.0]])]});}
            var Q12;
            {var subQ1=sQuery(id+"F2.wireOp",EDGE,"E52.2");Q12=makeQuery(id+"F2.imprint","IMPRINT",FACE,{"disambiguationData":[TD([[makeQuery(id+"F2.imprint","IMPRINT",EDGE,{"derivedFrom":subQ1}),1.0]])]});}
            var Q13;
            {var subQ6=sQuery(id+"F2.wireOp",EDGE,"E52.8");Q13=makeQuery(id+"F2.imprint","IMPRINT",FACE,{"disambiguationData":[TD([[makeQuery(id+"F2.imprint","IMPRINT",EDGE,{"derivedFrom":subQ6}),1.0]])]});}
            var Q14;
            {var subQ5=sQuery(id+"F2.wireOp",EDGE,"E52.6");Q14=makeQuery(id+"F2.imprint","IMPRINT",FACE,{"disambiguationData":[TD([[makeQuery(id+"F2.imprint","IMPRINT",EDGE,{"derivedFrom":subQ5}),1.0]])]});}
            var Q15;
            {var subQ5=sQuery(id+"F2.wireOp",EDGE,"E52.12");Q15=makeQuery(id+"F2.imprint","IMPRINT",FACE,{"disambiguationData":[TD([[makeQuery(id+"F2.imprint","IMPRINT",EDGE,{"derivedFrom":subQ5}),1.0]])]});}
            var Q16;
            {var subQ0=sQuery(id+"F2.wireOp",EDGE,"E52.13");var subQ1=makeQuery(id+"F2.imprint","INTERSECT",VERTEX,{"derivedFrom":[subQ0,sQuery(id+"F2.wireOp",EDGE,"E52.16")]});Q16=makeQuery(id+"F2.imprint","IMPRINT",FACE,{"disambiguationData":[TD([[makeQuery(id+"F2.imprint","IMPRINT",EDGE,{"disambiguationData":[TD([[subQ1,1.0]])],"derivedFrom":subQ0}),1.0]])]});}
            var Q17;
            {var subQ0=sQuery(id+"F2.wireOp",EDGE,"E52.15");var subQ1=sQuery(id+"F2.wireOp",EDGE,"E52.13");var subQ2=makeQuery(id+"F2.imprint","INTERSECT",VERTEX,{"derivedFrom":[subQ1,subQ0]});Q17=makeQuery(id+"F2.imprint","IMPRINT",FACE,{"disambiguationData":[TD([[makeQuery(id+"F2.imprint","IMPRINT",EDGE,{"disambiguationData":[TD([[subQ2,1.0]])],"derivedFrom":subQ1}),-1.0]])]});}
            var Q18;
            {var subQ0=sQuery(id+"F2.wireOp",EDGE,"E52.16");var subQ1=sQuery(id+"F2.wireOp",EDGE,"E52.13");var subQ2=makeQuery(id+"F2.imprint","INTERSECT",VERTEX,{"derivedFrom":[subQ1,subQ0]});Q18=makeQuery(id+"F2.imprint","IMPRINT",FACE,{"disambiguationData":[TD([[makeQuery(id+"F2.imprint","IMPRINT",EDGE,{"disambiguationData":[TD([[subQ2,1.0]])],"derivedFrom":subQ1}),-1.0]])]});}
            var Q19;
            {var subQ0=sQuery(id+"F2.wireOp",EDGE,"E52.16");var subQ1=sQuery(id+"F2.wireOp",EDGE,"E52.13");var subQ2=makeQuery(id+"F2.imprint","INTERSECT",VERTEX,{"derivedFrom":[subQ1,subQ0]});Q19=makeQuery(id+"F2.imprint","IMPRINT",FACE,{"disambiguationData":[TD([[makeQuery(id+"F2.imprint","IMPRINT",EDGE,{"disambiguationData":[TD([[subQ2,-1.0]])],"derivedFrom":subQ1}),-1.0]])]});}
            var Q20;
            {var subQ0=sQuery(id+"F2.wireOp",EDGE,"E52.14");var subQ1=sQuery(id+"F2.wireOp",EDGE,"E52.13");var subQ2=makeQuery(id+"F2.imprint","INTERSECT",VERTEX,{"derivedFrom":[subQ1,subQ0]});Q20=makeQuery(id+"F2.imprint","IMPRINT",FACE,{"disambiguationData":[TD([[makeQuery(id+"F2.imprint","IMPRINT",EDGE,{"disambiguationData":[TD([[subQ2,-1.0]])],"derivedFrom":subQ1}),-1.0]])]});}
            extrude(context, id + "F3", {"entities" : qUnion([Q0, Q1, Q2, Q3, Q4, Q5, Q6, Q7, Q8, Q9, Q10, Q11, Q12, Q13, Q14, Q15, Q16, Q17, Q18, Q19, Q20]), "operationType" : NewBodyOperationType.ADD, "depth" : 10 * mm});
        }
    });
